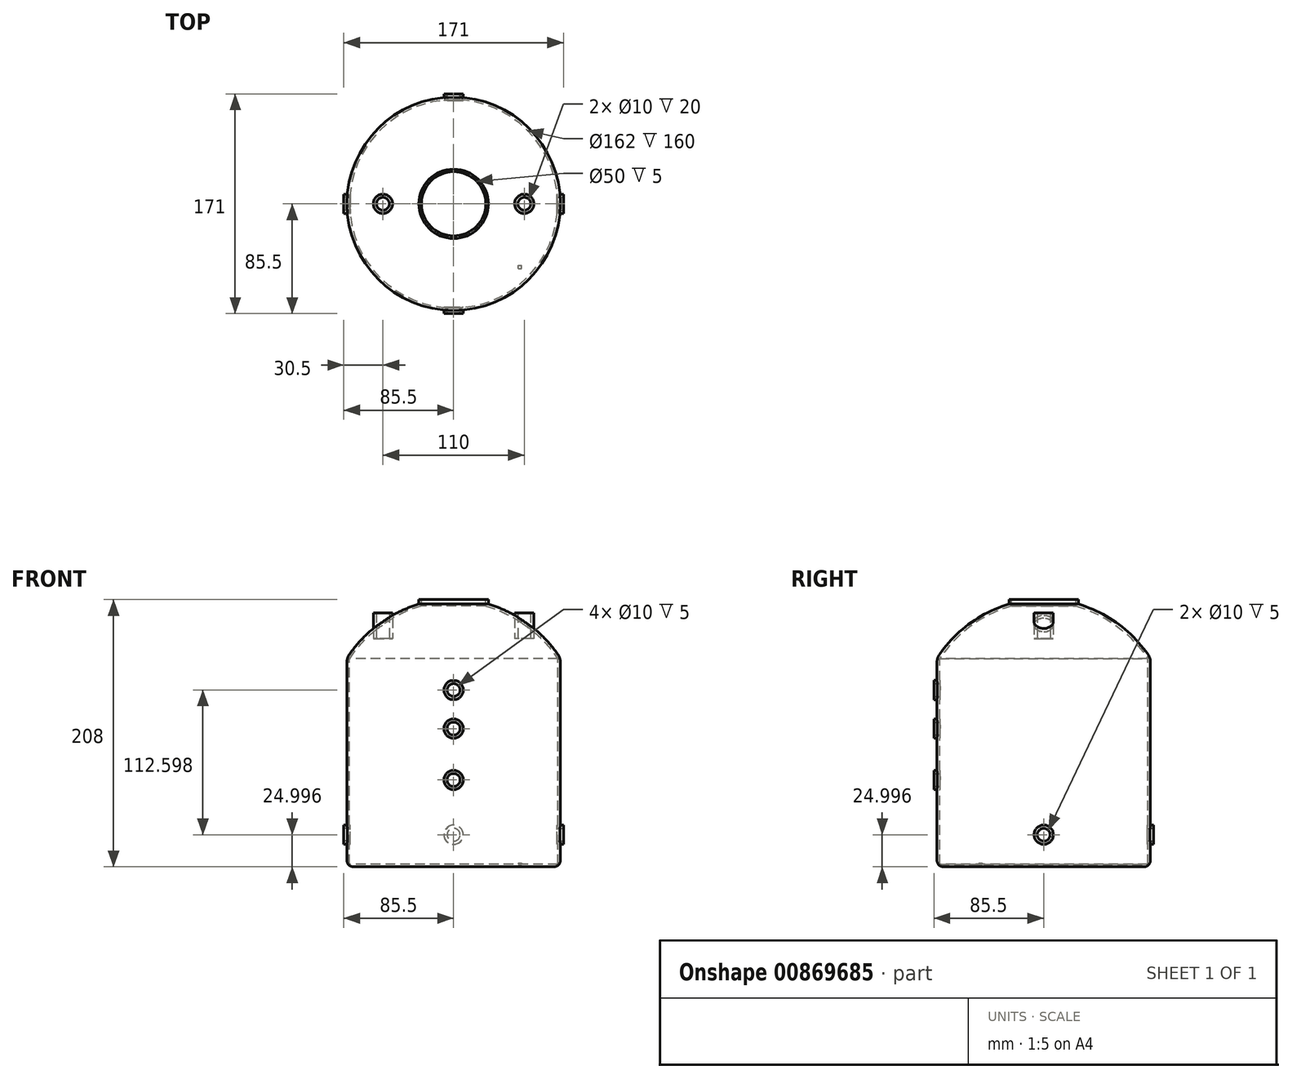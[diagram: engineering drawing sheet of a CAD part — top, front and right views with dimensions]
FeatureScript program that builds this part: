
annotation { "Feature Type Name" : "Feature", "Feature Type Description" : "" }
export const myFeature = defineFeature(function(context is Context, id is Id, definition is map)
    precondition{}
    {
        {
            var Q0;
            Q0=qCreatedBy(makeId("Front.planeOp"),FACE);
            var sketch = newSketch(context, id + "F0", { "sketchPlane" : qUnion([Q0])});
            skLineSegment(sketch, "E0", {"start": v(0, 99.97) * mm, "end": v(25, 99.97) * mm});
            skLineSegment(sketch, "E1", {"start": v(25, 99.97) * mm, "end": v(25, 94.97) * mm});
            skArc(sketch, "E2", {"start": v(81, 53.97) * mm, "mid": v(56.67, 79.48) * mm, "end": v(25, 94.97) * mm});
            skLineSegment(sketch, "E3", {"start": v(81, 53.97) * mm, "end": v(81, -106.03) * mm});
            skLineSegment(sketch, "E4", {"start": v(81, -106.03) * mm, "end": v(0, -106.03) * mm});
            skLineSegment(sketch, "E5", {"start": v(0, 99.97) * mm, "end": v(0, -106.03) * mm, "construction": true});
            skLineSegment(sketch, "E6", {"start": v(0, 99.97) * mm, "end": v(0, -106.03) * mm});
            skLineSegment(sketch, "E7", {"start": v(81, 53.97) * mm, "end": v(0, 53.97) * mm, "construction": true});
            skPoint(sketch, "E8", {"position": v(0, 53.97) * mm});
            skLineSegment(sketch, "E9", {"start": v(0, 29.4) * mm, "end": v(81, 29.4) * mm, "construction": true});
            skSolve(sketch);
        }
        {
            var Q0;
            Q0 = qSketchRegion(id + "F0", true);
            var Q1;
            Q1=sQuery(id+"F0.wireOp",EDGE,"E6");
            revolve(context, id + "F1", {"surfaceOperationType" : NewSurfaceOperationType.NEW, "entities" : qUnion([Q0]), "axis" : qUnion([Q1]), "revolveType" : RevolveType.FULL});
        }
        {
            var Q0;
            Q0=makeQuery(id+"F1.opRevolve","SWEPT_FACE",FACE,{"disambiguationData":[OSD([sQuery(id+"F0.wireOp",EDGE,"E0")])]});
            var sketch = newSketch(context, id + "F2", { "sketchPlane" : qUnion([Q0])});
            skCircle(sketch, "E10", {"center": v(0, 0) * mm, "radius": 25 * mm});
            skCircle(sketch, "E11", {"center": v(0, 0) * mm, "radius": 17.5 * mm});
            skSolve(sketch);
        }
        {
            var Q0;
            Q0=makeQuery(id+"F1.opRevolve","SWEPT_FACE",FACE,{"disambiguationData":[OSD([sQuery(id+"F0.wireOp",EDGE,"E0")])]});
            shell(context, id + "F3", {"entities" : qUnion([Q0]), "thickness" : 2 * mm, "oppositeDirection" : true});
        }
        {
            var Q0;
            Q0=qCreatedBy(makeId("Front.planeOp"),FACE);
            var sketch = newSketch(context, id + "F4", { "sketchPlane" : qUnion([Q0])});
            skLineSegment(sketch, "E12", {"start": v(0, 0) * mm, "end": v(0, 54.56) * mm, "construction": true});
            skLineSegment(sketch, "E13", {"start": v(0, 0) * mm, "end": v(0, -25) * mm, "construction": true});
            skLineSegment(sketch, "E14", {"start": v(0, -25) * mm, "end": v(0, -88.03) * mm, "construction": true});
            skLineSegment(sketch, "E15", {"start": v(0, -88.03) * mm, "end": v(0, -108.03) * mm, "construction": true});
            skLineSegment(sketch, "E16", {"start": v(0, 54.56) * mm, "end": v(0, 99.97) * mm});
            skLineSegment(sketch, "E17", {"start": v(0, 54.56) * mm, "end": v(0, 96.46) * mm, "construction": true});
            skPoint(sketch, "E18", {"position": v(0, 77.26) * mm});
            skSolve(sketch);
        }
        {
            var Q0;
            Q0=qCreatedBy(makeId("Top.planeOp"),FACE);
            var Q1;
            Q1=sQuery(id+"F4.wireOp",VERTEX,"E12.end");
            cPlane(context, id + "F5", {"entities" : qUnion([Q0, Q1]), "cplaneType" : CPlaneType.PLANE_POINT, "offset" : 25 * mm, "width" : 150 * mm, "height" : 150 * mm});
        }
        {
            var Q0;
            Q0=qCreatedBy(id+"F5.planeOp",FACE);
            var sketch = newSketch(context, id + "F6", { "sketchPlane" : qUnion([Q0])});
            skLineSegment(sketch, "E19", {"start": v(0, 83) * mm, "end": v(0, -83) * mm, "construction": true});
            skLineSegment(sketch, "E20", {"start": v(83, 0) * mm, "end": v(-83, 0) * mm, "construction": true});
            skSolve(sketch);
        }
        {
            var Q0;
            Q0=qCreatedBy(id+"F5.planeOp",FACE);
            cPlane(context, id + "F7", {"entities" : qUnion([Q0]), "cplaneType" : CPlaneType.OFFSET, "offset" : 7 * mm, "width" : 150 * mm, "height" : 150 * mm});
        }
        {
            var Q0;
            Q0=qCreatedBy(id+"F7.planeOp",FACE);
            var sketch = newSketch(context, id + "F8", { "sketchPlane" : qUnion([Q0])});
            skCircle(sketch, "E21", {"center": v(-43.5, 0) * mm, "radius": 5 * mm});
            skCircle(sketch, "E22", {"center": v(43.5, 0) * mm, "radius": 5 * mm});
            skCircle(sketch, "E23", {"center": v(0, 0) * mm, "radius": 43.5 * mm});
            skSolve(sketch);
        }
        {
            var Q0;
            Q0 = qSketchRegion(id + "F8", true);
            extrude(context, id + "F9", {"entities" : qUnion([Q0]), "operationType" : NewBodyOperationType.REMOVE, "oppositeDirection" : true, "depth" : 25 * mm, "offsetDistance" : 25 * mm, "symmetric" : true});
        }
        {
            var Q0;
            Q0=makeQuery(id+"F1.opRevolve","SWEPT_FACE",FACE,{"disambiguationData":[OSD([sQuery(id+"F0.wireOp",EDGE,"E4")])]});
            var sketch = newSketch(context, id + "F10", { "sketchPlane" : qUnion([Q0])});
            skLineSegment(sketch, "E24", {"start": v(-83, 0) * mm, "end": v(-83, -83) * mm, "construction": true});
            skLineSegment(sketch, "E25", {"start": v(-83, 0) * mm, "end": v(-83, 83) * mm, "construction": true});
            skCircle(sketch, "E26.0", {"center": v(0, 0) * mm, "radius": 83 * mm});
            skLineSegment(sketch, "E27", {"start": v(-83, 83) * mm, "end": v(83, 83) * mm, "construction": true});
            skLineSegment(sketch, "E28", {"start": v(0, 0) * mm, "end": v(0, 83) * mm, "construction": true});
            skLineSegment(sketch, "E29", {"start": v(83, 83) * mm, "end": v(83, -83) * mm, "construction": true});
            skLineSegment(sketch, "E30", {"start": v(0, 0) * mm, "end": v(83, 0) * mm, "construction": true});
            skLineSegment(sketch, "E31", {"start": v(83, -83) * mm, "end": v(-83, -83) * mm, "construction": true});
            skLineSegment(sketch, "E32", {"start": v(0, -83) * mm, "end": v(0, 0) * mm, "construction": true});
            skLineSegment(sketch, "E33", {"start": v(0, 0) * mm, "end": v(-83, 0) * mm, "construction": true});
            skSolve(sketch);
        }
        {
            var Q0;
            Q0=qCreatedBy(makeId("Front.planeOp"),FACE);
            var Q1;
            Q1=sQuery(id+"F10.wireOp",VERTEX,"E28.end");
            cPlane(context, id + "F11", {"entities" : qUnion([Q0, Q1]), "cplaneType" : CPlaneType.PLANE_POINT, "offset" : 25 * mm, "width" : 150 * mm, "height" : 150 * mm});
        }
        {
            var Q0;
            Q0=qCreatedBy(id+"F11.planeOp",FACE);
            var sketch = newSketch(context, id + "F12", { "sketchPlane" : qUnion([Q0])});
            skCircle(sketch, "E34", {"center": v(0, -40.44) * mm, "radius": 5 * mm});
            skCircle(sketch, "E35", {"center": v(0, -0.44) * mm, "radius": 5 * mm});
            skCircle(sketch, "E36", {"center": v(0, 29.56) * mm, "radius": 5 * mm});
            skSolve(sketch);
        }
        {
            var Q0;
            Q0 = qSketchRegion(id + "F12", true);
            extrude(context, id + "F13", {"entities" : qUnion([Q0]), "operationType" : NewBodyOperationType.REMOVE, "depth" : 25 * mm, "offsetDistance" : 25 * mm, "symmetric" : true});
        }
        {
            var Q0;
            Q0=qCreatedBy(id+"F11.planeOp",FACE);
            var sketch = newSketch(context, id + "F14", { "sketchPlane" : qUnion([Q0])});
            skLineSegment(sketch, "E37", {"start": v(0, 0) * mm, "end": v(0, -108.03) * mm, "construction": true});
            skLineSegment(sketch, "E38.0", {"start": v(83, -108.03) * mm, "end": v(-83, -108.03) * mm});
            skCircle(sketch, "E39", {"center": v(0, -40.44) * mm, "radius": 7.5 * mm});
            skCircle(sketch, "E40", {"center": v(0, -0.44) * mm, "radius": 7.5 * mm});
            skCircle(sketch, "E41", {"center": v(0, -0.44) * mm, "radius": 5 * mm});
            skCircle(sketch, "E42", {"center": v(0, -40.44) * mm, "radius": 5 * mm});
            skCircle(sketch, "E43", {"center": v(0, 29.56) * mm, "radius": 7.5 * mm});
            skCircle(sketch, "E44", {"center": v(0, 29.56) * mm, "radius": 5 * mm});
            skSolve(sketch);
        }
        {
            var Q0;
            Q0 = qSketchRegion(id + "F14", true);
            extrude(context, id + "F15", {"entities" : qUnion([Q0]), "operationType" : NewBodyOperationType.ADD, "depth" : 5 * mm, "offsetDistance" : 25 * mm, "symmetric" : true});
        }
        {
            var Q0;
            Q0=sQuery(id+"F10.wireOp",EDGE,"E29");
            cPlane(context, id + "F16", {"entities" : qUnion([Q0]), "cplaneType" : CPlaneType.LINE_ANGLE, "offset" : 25 * mm, "angle" : 90 * degree, "width" : 150 * mm, "height" : 150 * mm});
        }
        {
            var Q0;
            Q0=sQuery(id+"F10.wireOp",VERTEX,"E24.start");
            var Q1;
            Q1=qCreatedBy(id+"F16.planeOp",FACE);
            cPlane(context, id + "F17", {"entities" : qUnion([Q0, Q1]), "cplaneType" : CPlaneType.PLANE_POINT, "offset" : 25 * mm, "width" : 150 * mm, "height" : 150 * mm});
        }
        {
            var Q0;
            Q0=qCreatedBy(id+"F17.planeOp",FACE);
            var sketch = newSketch(context, id + "F18", { "sketchPlane" : qUnion([Q0])});
            skCircle(sketch, "E45", {"center": v(0, -83.03) * mm, "radius": 5 * mm});
            skSolve(sketch);
        }
        {
            var Q0;
            Q0=makeQuery(id+"F1.opRevolve","SWEPT_EDGE",EDGE,{"disambiguationData":[OSD([sQuery(id+"F0.wireOp",EDGE,"E2"),sQuery(id+"F0.wireOp",EDGE,"E3")])]});
            fillet(context, id + "F19", {"entities" : qUnion([Q0]), "radius" : 10 * mm, "tangentPropagation" : true, "allowEdgeOverflow" : false});
        }
        {
            var Q0;
            Q0=makeQuery(id+"F1.opRevolve","SWEPT_EDGE",EDGE,{"disambiguationData":[OSD([sQuery(id+"F0.wireOp",EDGE,"E3"),sQuery(id+"F0.wireOp",EDGE,"E4")])]});
            fillet(context, id + "F20", {"entities" : qUnion([Q0]), "radius" : 5 * mm, "tangentPropagation" : true, "allowEdgeOverflow" : false});
        }
        {
            var Q0;
            Q0=makeQuery(id+"F10.imprint","IMPRINT",FACE,{"disambiguationData":[TD([[makeQuery(id+"F10.imprint","IMPRINT",EDGE,{"derivedFrom":sQuery(id+"F10.wireOp",EDGE,"E26.0")}),-1.0]])]});
            var Q1;
            Q1=sQuery(id+"F2.wireOp",VERTEX,"E10.center");
            cPlane(context, id + "F21", {"entities" : qUnion([Q0, Q1]), "cplaneType" : CPlaneType.PLANE_POINT, "offset" : 25 * mm, "width" : 150 * mm, "height" : 150 * mm});
        }
        {
            var Q0;
            Q0=sQuery(id+"F6.wireOp",EDGE,"E20");
            cPoint(context, id + "F22", {"entities" : qUnion([Q0]), "parameter" : 0.5});
        }
        {
            var Q0;
            Q0=makeQuery(id+"F10.imprint","IMPRINT",FACE,{"disambiguationData":[TD([[makeQuery(id+"F10.imprint","IMPRINT",EDGE,{"derivedFrom":sQuery(id+"F10.wireOp",EDGE,"E26.0")}),-1.0]])]});
            var Q1;
            Q1 = qCreatedBy(id + "F22" ,VERTEX);
            cPlane(context, id + "F23", {"entities" : qUnion([Q0, Q1]), "cplaneType" : CPlaneType.PLANE_POINT, "offset" : 25 * mm, "width" : 150 * mm, "height" : 150 * mm});
        }
        {
            var Q0;
            Q0=qCreatedBy(id+"F23.planeOp",FACE);
            var sketch = newSketch(context, id + "F24", { "sketchPlane" : qUnion([Q0])});
            skCircle(sketch, "E46", {"center": v(0, 0) * mm, "radius": 55 * mm, "construction": true});
            skLineSegment(sketch, "E47", {"start": v(-83, 0) * mm, "end": v(83, 0) * mm, "construction": true});
            skPoint(sketch, "E48", {"position": v(-55, 0) * mm});
            skPoint(sketch, "E49", {"position": v(55, 0) * mm});
            skCircle(sketch, "E50", {"center": v(-55, 0) * mm, "radius": 5 * mm});
            skCircle(sketch, "E51", {"center": v(55, 0) * mm, "radius": 5 * mm});
            skSolve(sketch);
        }
        {
            var Q0;
            Q0 = qSketchRegion(id + "F24", true);
            var Q1;
            Q1=makeQuery(id+"F1.opRevolve","SWEPT_FACE",FACE,{"disambiguationData":[OSD([sQuery(id+"F0.wireOp",EDGE,"E4")])]});
            extrude(context, id + "F25", {"entities" : qUnion([Q0]), "operationType" : NewBodyOperationType.REMOVE, "oppositeDirection" : true, "depth" : 40 * mm, "endBoundEntityFace" : qUnion([Q1]), "offsetDistance" : 25 * mm});
        }
        {
            var Q0;
            Q0=qCreatedBy(id+"F17.planeOp",FACE);
            var sketch = newSketch(context, id + "F26", { "sketchPlane" : qUnion([Q0])});
            skLineSegment(sketch, "E52", {"start": v(83.23, 79.31) * mm, "end": v(-99.39, 79.31) * mm, "construction": true});
            skFitSpline(sketch, "E53.0", {"points": [v(-3.11, 80.21) * mm, v(-2.38, 79.89) * mm, v(-1.74, 79.7) * mm, v(-1.23, 79.58) * mm, v(-0.7, 79.5) * mm, v(-0.16, 79.47) * mm, v(0.39, 79.48) * mm, v(0.93, 79.53) * mm, v(1.45, 79.62) * mm, v(2.12, 79.8) * mm, v(2.72, 80.03) * mm, v(3.25, 80.32) * mm, v(3.6, 80.55) * mm, v(3.92, 80.8) * mm, v(4.3, 81.17) * mm, v(4.65, 81.64) * mm, v(4.92, 82.24) * mm, v(5.02, 82.85) * mm, v(4.97, 83.47) * mm, v(4.8, 83.96) * mm, v(4.57, 84.34) * mm, v(4.36, 84.62) * mm, v(4.1, 84.9) * mm, v(3.81, 85.14) * mm, v(3.48, 85.38) * mm, v(2.97, 85.67) * mm, v(2.4, 85.91) * mm, v(1.75, 86.1) * mm, v(1.24, 86.2) * mm, v(0.72, 86.28) * mm, v(-0.02, 86.32) * mm, v(-0.74, 86.28) * mm, v(-1.44, 86.17) * mm, v(-1.94, 86.05) * mm, v(-2.41, 85.9) * mm, v(-2.85, 85.72) * mm, v(-3.25, 85.52) * mm, v(-3.74, 85.21) * mm, v(-4.23, 84.8) * mm, v(-4.66, 84.23) * mm, v(-4.93, 83.64) * mm, v(-5.03, 83.03) * mm, v(-4.97, 82.42) * mm, v(-4.74, 81.8) * mm, v(-4.36, 81.23) * mm, v(-3.81, 80.69) * mm, v(-3.11, 80.21) * mm, v(-2.38, 79.89) * mm, v(-1.74, 79.7) * mm, v(-3.11, 80.21) * mm]});
            skPoint(sketch, "E54", {"position": v(0, 79.48) * mm});
            skSolve(sketch);
        }
        {
            var Q0;
            Q0=qCreatedBy(id+"F5.planeOp",FACE);
            var Q1;
            Q1=sQuery(id+"F26.wireOp",VERTEX,"E54");
            cPlane(context, id + "F27", {"entities" : qUnion([Q0, Q1]), "cplaneType" : CPlaneType.PLANE_POINT, "offset" : 25 * mm, "width" : 150 * mm, "height" : 150 * mm});
        }
        {
            var Q0;
            Q0=qCreatedBy(id+"F27.planeOp",FACE);
            var sketch = newSketch(context, id + "F28", { "sketchPlane" : qUnion([Q0])});
            skCircle(sketch, "E55", {"center": v(0, 0) * mm, "radius": 55 * mm, "construction": true});
            skPoint(sketch, "E56", {"position": v(-55, 0) * mm});
            skPoint(sketch, "E57", {"position": v(55, 0) * mm});
            skCircle(sketch, "E58", {"center": v(-55, 0) * mm, "radius": 5 * mm});
            skCircle(sketch, "E59", {"center": v(-55, 0) * mm, "radius": 7.5 * mm});
            skCircle(sketch, "E60", {"center": v(55, 0) * mm, "radius": 5 * mm});
            skCircle(sketch, "E61", {"center": v(55, 0) * mm, "radius": 7.5 * mm});
            skSolve(sketch);
        }
        {
            var Q0;
            Q0 = qSketchRegion(id + "F28", true);
            extrude(context, id + "F29", {"entities" : qUnion([Q0]), "operationType" : NewBodyOperationType.ADD, "depth" : 20 * mm, "offsetDistance" : 25 * mm, "symmetric" : true});
        }
        {
            var Q0;
            Q0 = qSketchRegion(id + "F18", true);
            extrude(context, id + "F30", {"entities" : qUnion([Q0]), "operationType" : NewBodyOperationType.REMOVE, "endBound" : BoundingType.UP_TO_NEXT, "depth" : 25 * mm, "offsetDistance" : 25 * mm});
        }
        {
            var Q0;
            Q0=qCreatedBy(id+"F17.planeOp",FACE);
            var sketch = newSketch(context, id + "F31", { "sketchPlane" : qUnion([Q0])});
            skCircle(sketch, "E62.0", {"center": v(0, -83.03) * mm, "radius": 5 * mm});
            skCircle(sketch, "E63", {"center": v(0, -83.03) * mm, "radius": 7.5 * mm});
            skSolve(sketch);
        }
        {
            var Q0;
            Q0 = qSketchRegion(id + "F31", true);
            extrude(context, id + "F32", {"entities" : qUnion([Q0]), "operationType" : NewBodyOperationType.ADD, "oppositeDirection" : true, "depth" : 5 * mm, "offsetDistance" : 25 * mm, "symmetric" : true});
        }
        {
            var Q0;
            Q0=qCreatedBy(id+"F16.planeOp",FACE);
            var sketch = newSketch(context, id + "F33", { "sketchPlane" : qUnion([Q0])});
            skCircle(sketch, "E64", {"center": v(0, -83.03) * mm, "radius": 5 * mm});
            skSolve(sketch);
        }
        {
            var Q0;
            Q0 = qSketchRegion(id + "F33", true);
            extrude(context, id + "F34", {"entities" : qUnion([Q0]), "operationType" : NewBodyOperationType.REMOVE, "endBound" : BoundingType.UP_TO_NEXT, "oppositeDirection" : true, "depth" : 25 * mm, "offsetDistance" : 25 * mm});
        }
        {
            var Q0;
            Q0=qCreatedBy(id+"F16.planeOp",FACE);
            var sketch = newSketch(context, id + "F35", { "sketchPlane" : qUnion([Q0])});
            skCircle(sketch, "E65", {"center": v(0, -83.03) * mm, "radius": 7.5 * mm});
            skCircle(sketch, "E66", {"center": v(0, -83.03) * mm, "radius": 5 * mm});
            skSolve(sketch);
        }
        {
            var Q0;
            Q0 = qSketchRegion(id + "F35", true);
            extrude(context, id + "F36", {"entities" : qUnion([Q0]), "operationType" : NewBodyOperationType.ADD, "depth" : 5 * mm, "offsetDistance" : 25 * mm, "symmetric" : true});
        }
        {
            var Q0;
            Q0=sQuery(id+"F6.wireOp",VERTEX,"E19.start");
            var Q1;
            Q1=sQuery(id+"F10.wireOp",VERTEX,"E24.end");
            var Q2;
            Q2=sQuery(id+"F10.wireOp",VERTEX,"E29.end");
            cPlane(context, id + "F37", {"entities" : qUnion([Q0, Q1, Q2]), "cplaneType" : CPlaneType.THREE_POINT, "offset" : 25 * mm, "width" : 150 * mm, "height" : 150 * mm});
        }
        {
            var Q0;
            Q0=qCreatedBy(id+"F37.planeOp",FACE);
            var sketch = newSketch(context, id + "F38", { "sketchPlane" : qUnion([Q0])});
            skCircle(sketch, "E67", {"center": v(0, -83.03) * mm, "radius": 5 * mm});
            skSolve(sketch);
        }
        {
            var Q0;
            Q0 = qSketchRegion(id + "F38", true);
            extrude(context, id + "F39", {"entities" : qUnion([Q0]), "operationType" : NewBodyOperationType.REMOVE, "endBound" : BoundingType.UP_TO_NEXT, "oppositeDirection" : true, "depth" : 25 * mm, "offsetDistance" : 25 * mm});
        }
        {
            var Q0;
            Q0=qCreatedBy(id+"F37.planeOp",FACE);
            var sketch = newSketch(context, id + "F40", { "sketchPlane" : qUnion([Q0])});
            skCircle(sketch, "E68", {"center": v(0, -83.03) * mm, "radius": 5 * mm});
            skCircle(sketch, "E69", {"center": v(0, -83.03) * mm, "radius": 7.5 * mm});
            skSolve(sketch);
        }
        {
            var Q0;
            Q0 = qSketchRegion(id + "F40", true);
            extrude(context, id + "F41", {"entities" : qUnion([Q0]), "operationType" : NewBodyOperationType.ADD, "depth" : 5 * mm, "offsetDistance" : 25 * mm, "symmetric" : true});
        }
        {
            var Q0;
            Q0=makeQuery(id+"F10.imprint","IMPRINT",FACE,{"disambiguationData":[TD([[makeQuery(id+"F10.imprint","IMPRINT",EDGE,{"derivedFrom":sQuery(id+"F10.wireOp",EDGE,"E26.0")}),-1.0]])]});
            var sketch = newSketch(context, id + "F42", { "sketchPlane" : qUnion([Q0])});
            skCircle(sketch, "E70.0", {"center": v(0, 0) * mm, "radius": 78 * mm, "construction": true});
            skLineSegment(sketch, "E71.MirrorCS", {"start": v(0, 0) * mm, "end": v(-88.17, 88.17) * mm, "construction": true});
            skLineSegment(sketch, "E72", {"start": v(0, 0) * mm, "end": v(0, -78) * mm, "construction": true});
            skLineSegment(sketch, "E73", {"start": v(0, 0) * mm, "end": v(78, 0) * mm, "construction": true});
            skLineSegment(sketch, "E74", {"start": v(0, 0) * mm, "end": v(-78, 0) * mm, "construction": true});
            skLineSegment(sketch, "E75.MirrorCS", {"start": v(0, 0) * mm, "end": v(88.17, -88.17) * mm, "construction": true});
            skLineSegment(sketch, "E76.MirrorCS", {"start": v(0, 0) * mm, "end": v(-88.17, -88.17) * mm, "construction": true});
            skLineSegment(sketch, "E77.bottom", {"start": v(50.37, 50.37) * mm, "end": v(52.87, 50.37) * mm});
            skLineSegment(sketch, "E77.top", {"start": v(50.37, 47.87) * mm, "end": v(52.87, 47.87) * mm});
            skLineSegment(sketch, "E77.left", {"start": v(50.37, 50.37) * mm, "end": v(50.37, 47.87) * mm});
            skLineSegment(sketch, "E77.right", {"start": v(52.87, 50.37) * mm, "end": v(52.87, 47.87) * mm});
            skPoint(sketch, "E78", {"position": v(51.62, 49.12) * mm});
            skLineSegment(sketch, "E79", {"start": v(51.62, 49.12) * mm, "end": v(51.62, -58.48) * mm, "construction": true});
            skLineSegment(sketch, "E80", {"start": v(57.16, 49.12) * mm, "end": v(48.83, 49.12) * mm});
            skLineSegment(sketch, "E81", {"start": v(52.87, 50.37) * mm, "end": v(50.37, 47.87) * mm, "construction": true});
            skLineSegment(sketch, "E82", {"start": v(52.87, 47.87) * mm, "end": v(50.37, 50.37) * mm, "construction": true});
            skSolve(sketch);
        }
        {
            var Q0;
            Q0 = qSketchRegion(id + "F42", true);
            extrude(context, id + "F43", {"entities" : qUnion([Q0]), "operationType" : NewBodyOperationType.ADD, "oppositeDirection" : true, "depth" : 3 * mm, "offsetDistance" : 25 * mm});
        }
    });
